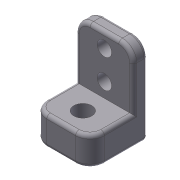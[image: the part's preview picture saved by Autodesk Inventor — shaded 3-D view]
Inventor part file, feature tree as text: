
AUTODESK INVENTOR PART (.ipt)
format: ipt  version: 2012 (Build 160160000, 160)  size: 177,152 bytes
history: native  units: in
note: dims shown in document units (in); Inventor stores cm internally (conversion verified against a paired STEP export)
features: extrude x5, sketch x5, fillet x2
ambient origin geometry x8: Origin, YZ Plane, XZ Plane, XY Plane, X Axis, Y Axis, Z Axis, Center Point
bodies: Solid1 (feature_tree)
feature tree (12):
  extrude  "Extrusion1"  Depth=1.0in
  extrude  "Extrusion4"  Depth=0.25in
  extrude  "Extrusion3"  Depth=0.5in
  extrude  "Extrusion5"  Depth=1.0in TaperAngle=0.0deg
  fillet  "Fillet4"  Radius=0.5in
  fillet  "Fillet5"  Radius=0.25in
  extrude  "Extrusion6"  Depth=1.0in TaperAngle=0.0deg
  sketch  "Sketch1"  dims[d0=1.5in d1=1.0in]
  sketch  "Sketch3"  dims[d2=1.0in d3=0.0in d11=0.25in]
  sketch  "Sketch4"  dims[d12=0.25in d13=0.5in]
  sketch  "Sketch5"  dims[d14=0.5in d15=1.0in d16=0.0in d22=0.5in d23=0.25in]
  sketch  "Sketch6"  dims[d24=0.5in d25=1.0in d26=0.0in d27=0.375in d28=0.3125in d29=0.5in d30=1.0in d31=0.0in d32=0.0625in d33=0.25in d34=0.1in d35=0.0in]
